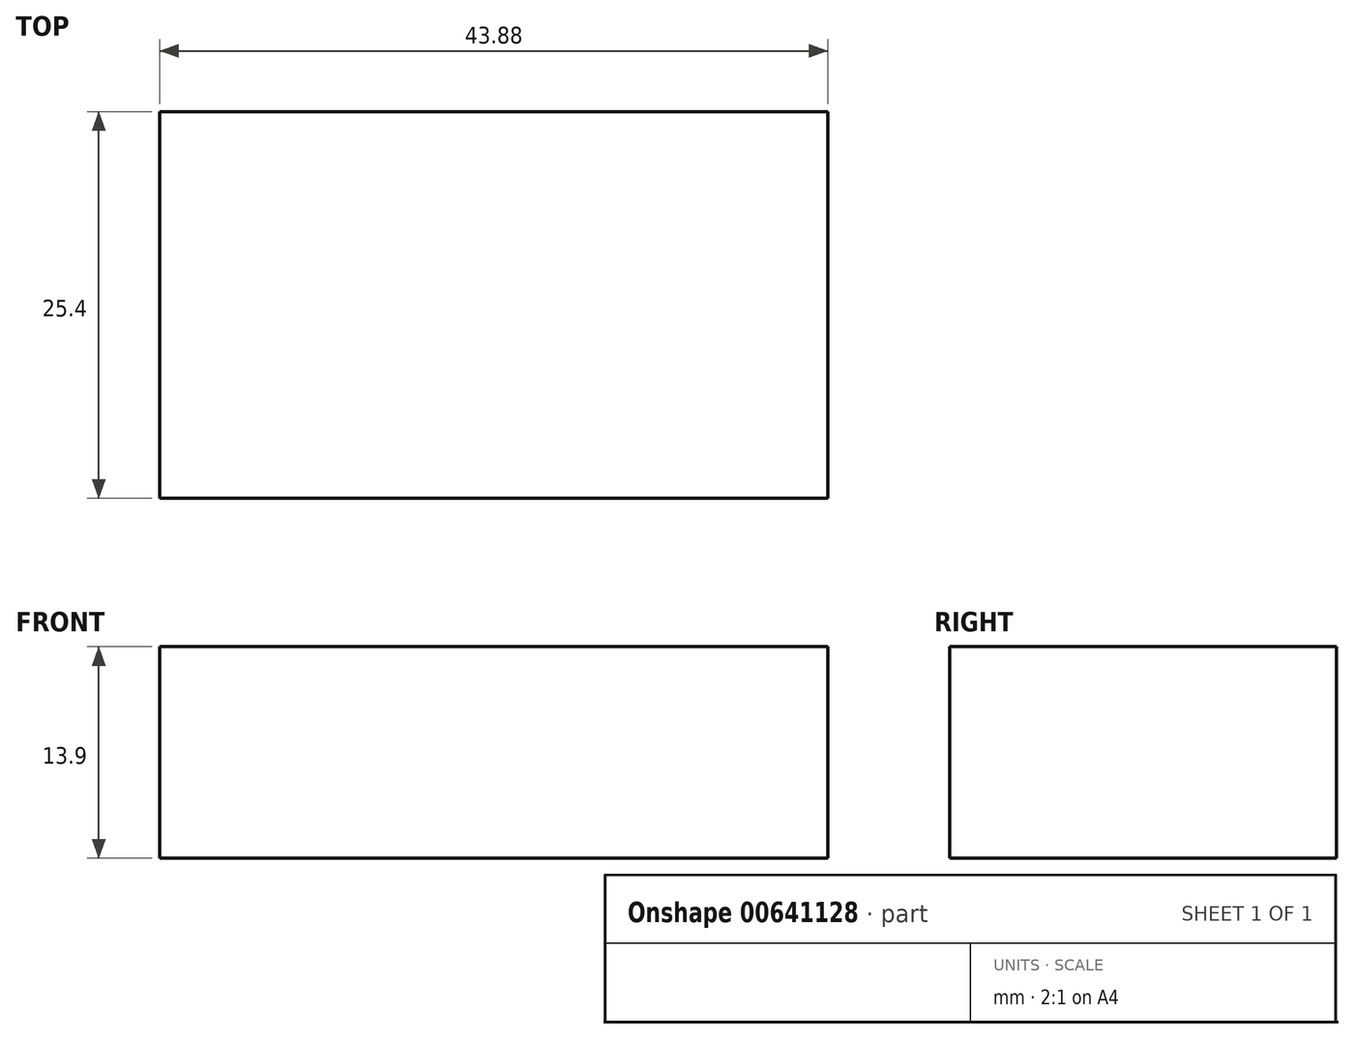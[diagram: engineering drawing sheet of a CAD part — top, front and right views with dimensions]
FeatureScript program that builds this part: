
annotation { "Feature Type Name" : "Feature", "Feature Type Description" : "" }
export const myFeature = defineFeature(function(context is Context, id is Id, definition is map)
    precondition{}
    {
        {
            var Q0;
            Q0=qCreatedBy(makeId("Front.planeOp"),FACE);
            var sketch = newSketch(context, id + "F0", { "sketchPlane" : qUnion([Q0])});
            skLineSegment(sketch, "E0.bottom", {"start": v(-20.72, 0) * mm, "end": v(23.16, 0) * mm});
            skLineSegment(sketch, "E0.top", {"start": v(-20.72, 13.9) * mm, "end": v(23.16, 13.9) * mm});
            skLineSegment(sketch, "E0.left", {"start": v(-20.72, 0) * mm, "end": v(-20.72, 13.9) * mm});
            skLineSegment(sketch, "E0.right", {"start": v(23.16, 0) * mm, "end": v(23.16, 13.9) * mm});
            skSolve(sketch);
        }
        {
            var Q0;
            Q0 = qSketchRegion(id + "F0", true);
            extrude(context, id + "F1", {"entities" : qUnion([Q0]), "depth" : 25.4 * mm, "offsetDistance" : 25.4 * mm});
        }
    });
